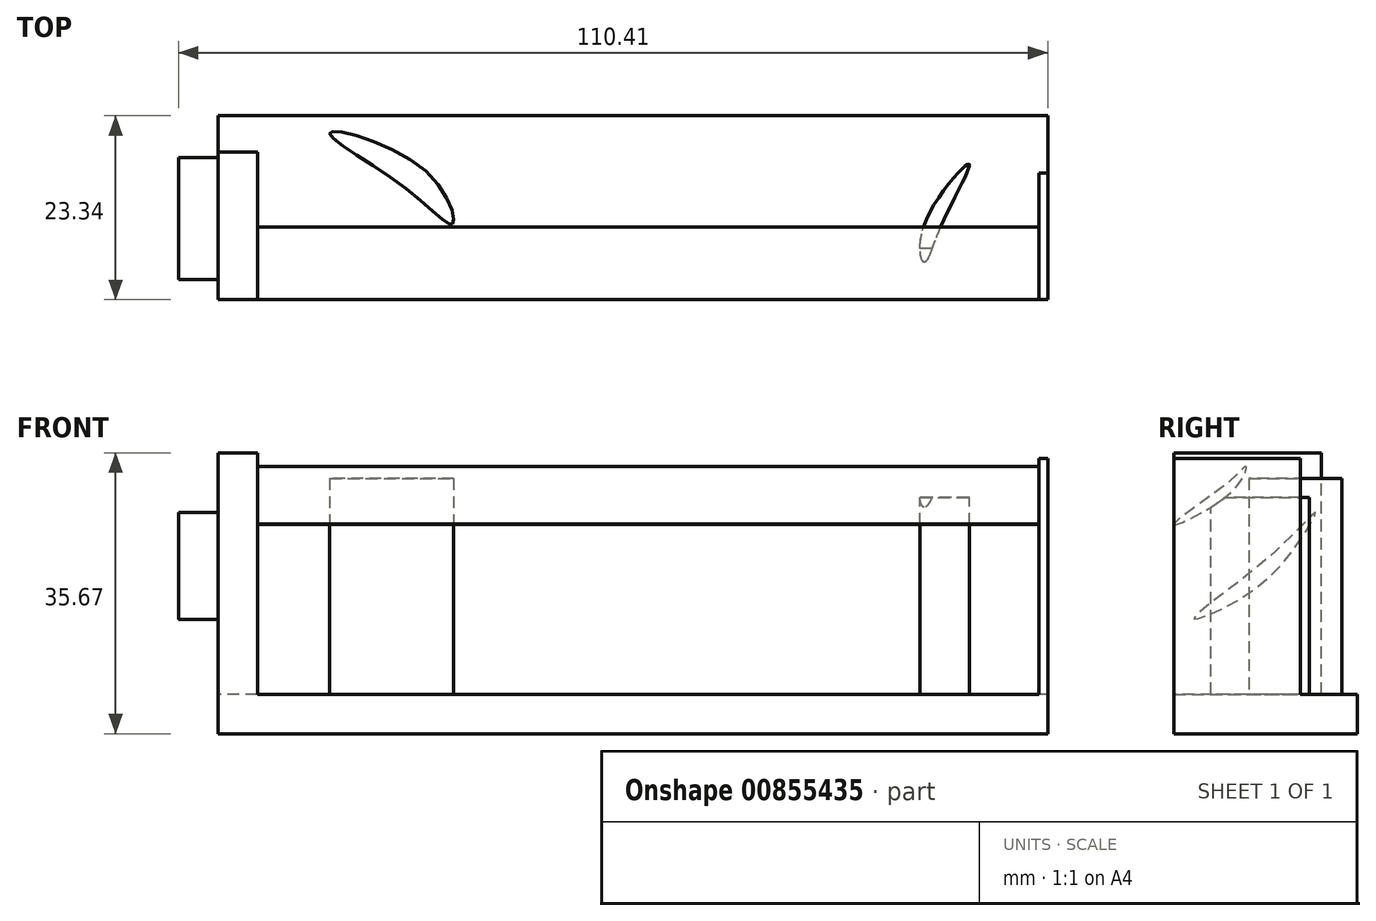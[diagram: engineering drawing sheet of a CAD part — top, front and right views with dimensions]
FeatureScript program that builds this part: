
annotation { "Feature Type Name" : "Feature", "Feature Type Description" : "" }
export const myFeature = defineFeature(function(context is Context, id is Id, definition is map)
    precondition{}
    {
        {
            var Q0;
            Q0=qCreatedBy(makeId("Top.planeOp"),FACE);
            var sketch = newSketch(context, id + "F0", { "sketchPlane" : qUnion([Q0])});
            skLineSegment(sketch, "E0.bottom", {"start": v(-29.79, -33.32) * mm, "end": v(75.62, -33.32) * mm});
            skLineSegment(sketch, "E0.top", {"start": v(-29.79, -56.66) * mm, "end": v(75.62, -56.66) * mm});
            skLineSegment(sketch, "E0.left", {"start": v(-29.79, -33.32) * mm, "end": v(-29.79, -56.66) * mm});
            skLineSegment(sketch, "E0.right", {"start": v(75.62, -33.32) * mm, "end": v(75.62, -56.66) * mm});
            skPoint(sketch, "E0.middle", {"position": v(22.92, -45) * mm});
            skSolve(sketch);
        }
        {
            var Q0;
            Q0=makeQuery(id+"F0.imprint","IMPRINT",FACE,{"disambiguationData":[TD([[makeQuery(id+"F0.imprint","IMPRINT",EDGE,{"derivedFrom":sQuery(id+"F0.wireOp",EDGE,"E0.bottom")}),-1.0]])]});
            var sketch = newSketch(context, id + "F1", { "sketchPlane" : qUnion([Q0])});
            skFitSpline(sketch, "E1", {"points": [v(59.91, -51.96) * mm, v(59.86, -47.36) * mm, v(65.6, -39.47) * mm, v(61.97, -47.48) * mm, v(59.91, -51.96) * mm]});
            skSolve(sketch);
        }
        {
            var Q0;
            Q0=makeQuery(id+"F1.imprint","IMPRINT",FACE,{"disambiguationData":[TD([[makeQuery(id+"F1.imprint","IMPRINT",EDGE,{"derivedFrom":sQuery(id+"F1.wireOp",EDGE,"E1")}),-1.0]])]});
            extrude(context, id + "F2", {"entities" : qUnion([Q0]), "depth" : 30 * mm, "offsetDistance" : 25.4 * mm});
        }
        {
            var Q0;
            Q0=makeQuery(id+"F0.imprint","IMPRINT",FACE,{"disambiguationData":[TD([[makeQuery(id+"F0.imprint","IMPRINT",EDGE,{"derivedFrom":sQuery(id+"F0.wireOp",EDGE,"E0.bottom")}),-1.0]])]});
            extrude(context, id + "F3", {"entities" : qUnion([Q0]), "operationType" : NewBodyOperationType.ADD, "depth" : 5 * mm, "offsetDistance" : 25.4 * mm});
        }
        {
            var Q0;
            Q0=makeQuery(id+"F3.opExtrude","CAP_FACE",FACE,{"disambiguationData":[OSD([sQuery(id+"F0.wireOp",EDGE,"E0.bottom"),sQuery(id+"F0.wireOp",EDGE,"E0.top"),sQuery(id+"F0.wireOp",EDGE,"E0.left"),sQuery(id+"F0.wireOp",EDGE,"E0.right")])],"isStart":false});
            var sketch = newSketch(context, id + "F4", { "sketchPlane" : qUnion([Q0])});
            skLineSegment(sketch, "E2.bottom", {"start": v(75.62, -56.66) * mm, "end": v(74.47, -56.66) * mm});
            skLineSegment(sketch, "E2.top", {"start": v(75.62, -40.6) * mm, "end": v(74.47, -40.6) * mm});
            skLineSegment(sketch, "E2.left", {"start": v(75.62, -56.66) * mm, "end": v(75.62, -40.6) * mm});
            skLineSegment(sketch, "E2.right", {"start": v(74.47, -56.66) * mm, "end": v(74.47, -40.6) * mm});
            skSolve(sketch);
        }
        {
            var Q0;
            Q0=makeQuery(id+"F4.imprint","IMPRINT",FACE,{"disambiguationData":[TD([[makeQuery(id+"F4.imprint","IMPRINT",EDGE,{"derivedFrom":sQuery(id+"F4.wireOp",EDGE,"E2.bottom")}),1.0]])]});
            extrude(context, id + "F5", {"entities" : qUnion([Q0]), "operationType" : NewBodyOperationType.ADD, "depth" : 30 * mm, "offsetDistance" : 25.4 * mm});
        }
        {
            var Q0;
            Q0=makeQuery(id+"F3.opExtrude","SWEPT_FACE",FACE,{"disambiguationData":[OSD([sQuery(id+"F0.wireOp",EDGE,"E0.left")])]});
            var sketch = newSketch(context, id + "F6", { "sketchPlane" : qUnion([Q0])});
            skLineSegment(sketch, "E3.bottom", {"start": v(56.66, 0) * mm, "end": v(37.94, 0) * mm});
            skLineSegment(sketch, "E3.top", {"start": v(56.66, 35.67) * mm, "end": v(37.94, 35.67) * mm});
            skLineSegment(sketch, "E3.left", {"start": v(56.66, 0) * mm, "end": v(56.66, 35.67) * mm});
            skLineSegment(sketch, "E3.right", {"start": v(37.94, 0) * mm, "end": v(37.94, 35.67) * mm});
            skSolve(sketch);
        }
        {
            var Q0;
            {var subQ0=sQuery(id+"F6.wireOp",EDGE,"E3.top");Q0=makeQuery(id+"F6.imprint","IMPRINT",FACE,{"disambiguationData":[TD([[makeQuery(id+"F6.imprint","IMPRINT",EDGE,{"derivedFrom":subQ0}),1.0]])]});}
            extrude(context, id + "F7", {"entities" : qUnion([Q0]), "operationType" : NewBodyOperationType.ADD, "oppositeDirection" : true, "depth" : 5 * mm, "offsetDistance" : 25.4 * mm});
        }
        {
            var Q0;
            {var subQ0=sQuery(id+"F0.wireOp",EDGE,"E0.left");Q0=makeQuery(id+"F7.boolean.opBoolean","MERGE",FACE,{"derivedFrom":[makeQuery(id+"F3.opExtrude","SWEPT_FACE",FACE,{"disambiguationData":[OSD([subQ0])]}),makeQuery(id+"F7.opExtrude","CAP_FACE",FACE,{"disambiguationData":[OSD([subQ0,sQuery(id+"F6.wireOp",EDGE,"E3.top"),sQuery(id+"F6.wireOp",EDGE,"E3.left"),sQuery(id+"F6.wireOp",EDGE,"E3.right")])],"isStart":true})]});}
            var sketch = newSketch(context, id + "F8", { "sketchPlane" : qUnion([Q0])});
            skFitSpline(sketch, "E4", {"points": [v(54.12, 14.6) * mm, v(48.42, 17.03) * mm, v(41.3, 23.61) * mm, v(38.64, 28.08) * mm, v(44, 22.96) * mm, v(54.12, 14.6) * mm]});
            skSolve(sketch);
        }
        {
            var Q0;
            Q0=makeQuery(id+"F8.imprint","IMPRINT",FACE,{"disambiguationData":[TD([[makeQuery(id+"F8.imprint","IMPRINT",EDGE,{"derivedFrom":sQuery(id+"F8.wireOp",EDGE,"E4")}),-1.0]])]});
            extrude(context, id + "F9", {"entities" : qUnion([Q0]), "operationType" : NewBodyOperationType.ADD, "depth" : 5 * mm, "offsetDistance" : 25.4 * mm});
        }
        {
            var Q0;
            Q0=makeQuery(id+"F3.opExtrude","CAP_FACE",FACE,{"disambiguationData":[OSD([sQuery(id+"F0.wireOp",EDGE,"E0.bottom"),sQuery(id+"F0.wireOp",EDGE,"E0.top"),sQuery(id+"F0.wireOp",EDGE,"E0.left"),sQuery(id+"F0.wireOp",EDGE,"E0.right")])],"isStart":false});
            var sketch = newSketch(context, id + "F10", { "sketchPlane" : qUnion([Q0])});
            skFitSpline(sketch, "E5", {"points": [v(0, -47.07) * mm, v(-3.5, -40.26) * mm, v(-15.6, -35.47) * mm, v(-5.63, -42.78) * mm, v(0, -47.07) * mm]});
            skSolve(sketch);
        }
        {
            var Q0;
            Q0=makeQuery(id+"F10.imprint","IMPRINT",FACE,{"disambiguationData":[TD([[makeQuery(id+"F10.imprint","IMPRINT",EDGE,{"derivedFrom":sQuery(id+"F10.wireOp",EDGE,"E5")}),1.0]])]});
            extrude(context, id + "F11", {"entities" : qUnion([Q0]), "operationType" : NewBodyOperationType.ADD, "depth" : 27.46 * mm, "offsetDistance" : 25.4 * mm});
        }
        {
            var Q0;
            Q0=makeQuery(id+"F7.opExtrude","CAP_FACE",FACE,{"disambiguationData":[OSD([sQuery(id+"F0.wireOp",EDGE,"E0.left"),sQuery(id+"F6.wireOp",EDGE,"E3.top"),sQuery(id+"F6.wireOp",EDGE,"E3.left"),sQuery(id+"F6.wireOp",EDGE,"E3.right")])],"isStart":false});
            var sketch = newSketch(context, id + "F12", { "sketchPlane" : qUnion([Q0])});
            skFitSpline(sketch, "E6", {"points": [v(-56.66, 26.6) * mm, v(-49.2, 30.86) * mm, v(-47.47, 33.95) * mm, v(-49.3, 32.33) * mm, v(-56.66, 26.6) * mm]});
            skSolve(sketch);
        }
        {
            var Q0;
            {var subQ0=sQuery(id+"F12.wireOp",EDGE,"E6");var subQ1=makeQuery(id+"F7.opExtrude","CAP_EDGE",EDGE,{"disambiguationData":[OSD([sQuery(id+"F6.wireOp",EDGE,"E3.left")])],"isStart":false});var subQ2=makeQuery(id+"F12.imprint","INTERSECT",VERTEX,{"disambiguationData":[OD(0.0)],"derivedFrom":[subQ1,subQ0]});Q0=makeQuery(id+"F12.imprint","IMPRINT",FACE,{"disambiguationData":[TD([[makeQuery(id+"F12.imprint","IMPRINT",EDGE,{"disambiguationData":[TD([[subQ2,1.0]])],"derivedFrom":subQ0}),1.0]])]});}
            extrude(context, id + "F13", {"entities" : qUnion([Q0]), "operationType" : NewBodyOperationType.ADD, "depth" : 100 * mm, "offsetDistance" : 25.4 * mm});
        }
    });
